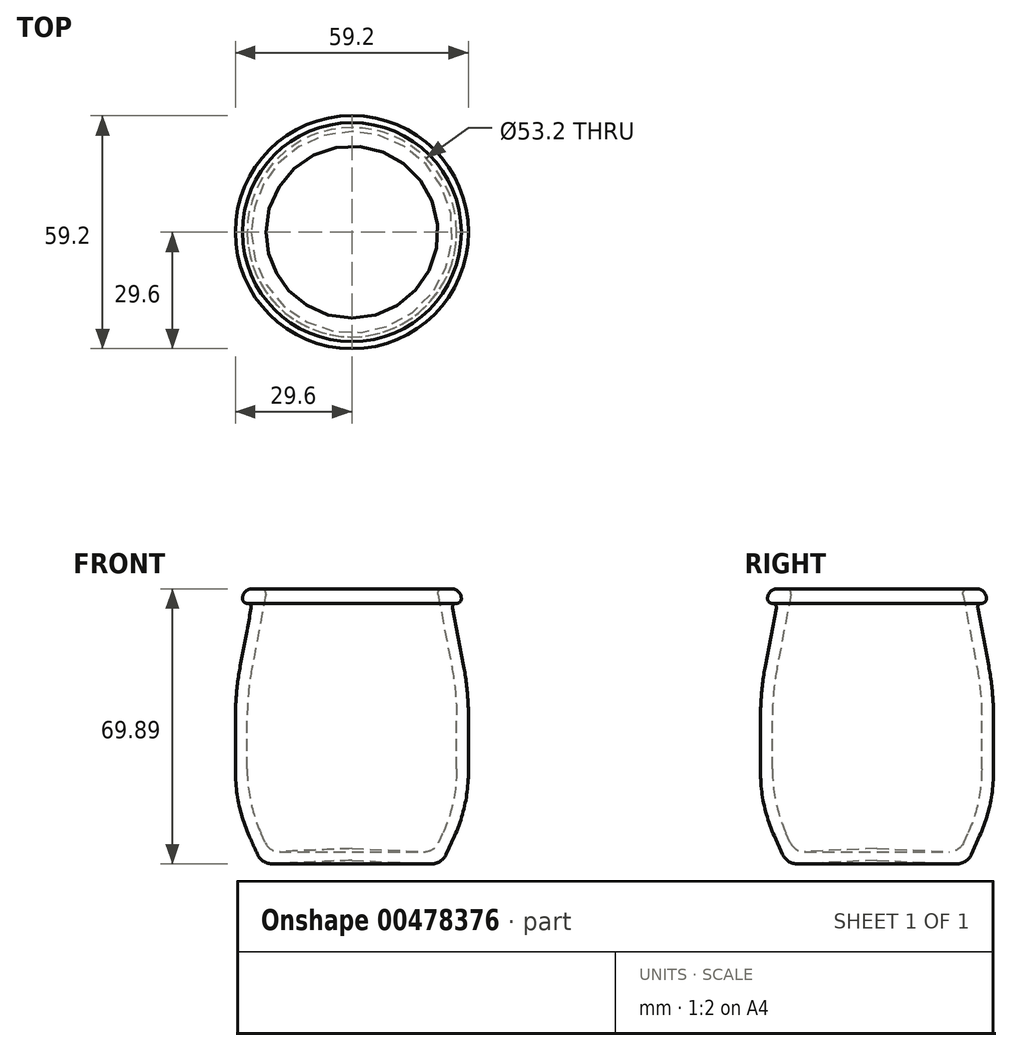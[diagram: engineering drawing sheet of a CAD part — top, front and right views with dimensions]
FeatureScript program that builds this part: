
annotation { "Feature Type Name" : "Feature", "Feature Type Description" : "" }
export const myFeature = defineFeature(function(context is Context, id is Id, definition is map)
    precondition{}
    {
        {
            var Q0;
            Q0=qCreatedBy(makeId("Front.planeOp"),FACE);
            var sketch = newSketch(context, id + "F0", { "sketchPlane" : qUnion([Q0])});
            skLineSegment(sketch, "E0.bottom", {"start": v(-27.8, 70) * mm, "end": v(-21.6, 70) * mm});
            skLineSegment(sketch, "E0.top", {"start": v(-27.8, 66.3) * mm, "end": v(-25.35, 66.3) * mm});
            skLineSegment(sketch, "E0.left", {"start": v(-27.8, 70) * mm, "end": v(-27.8, 66.3) * mm});
            skLineSegment(sketch, "E0.right", {"start": v(27.8, 70) * mm, "end": v(27.8, 66.3) * mm});
            skLineSegment(sketch, "E1.left", {"start": v(-29.6, 43.9) * mm, "end": v(-29.6, 15) * mm});
            skLineSegment(sketch, "E1.right", {"start": v(29.6, 43.9) * mm, "end": v(29.6, 15) * mm});
            skLineSegment(sketch, "E2", {"start": v(-25.35, 66.3) * mm, "end": v(-29.6, 43.9) * mm});
            skLineSegment(sketch, "E3", {"start": v(25.35, 66.3) * mm, "end": v(29.6, 43.9) * mm});
            skLineSegment(sketch, "E4", {"start": v(-29.6, 15) * mm, "end": v(-22.85, 0) * mm});
            skLineSegment(sketch, "E5", {"start": v(22.85, 0) * mm, "end": v(29.6, 15) * mm});
            skLineSegment(sketch, "E6.trimOffspring", {"start": v(25.35, 66.3) * mm, "end": v(27.8, 66.3) * mm});
            skLineSegment(sketch, "E7", {"start": v(0, 70) * mm, "end": v(0, 1) * mm, "construction": true});
            skLineSegment(sketch, "E8", {"start": v(-22.85, 0) * mm, "end": v(0, 1) * mm});
            skLineSegment(sketch, "E9", {"start": v(0, 1) * mm, "end": v(22.85, 0) * mm});
            skLineSegment(sketch, "E10.0", {"start": v(-21.6, 70) * mm, "end": v(-26.6, 43.62) * mm});
            skLineSegment(sketch, "E10.1", {"start": v(-26.6, 43.62) * mm, "end": v(-26.6, 15.64) * mm});
            skLineSegment(sketch, "E10.3", {"start": v(-26.6, 15.64) * mm, "end": v(-20.95, 3.09) * mm});
            skLineSegment(sketch, "E10.4", {"start": v(-20.95, 3.09) * mm, "end": v(0, 4) * mm});
            skLineSegment(sketch, "E10.5", {"start": v(21.6, 70) * mm, "end": v(26.6, 43.62) * mm});
            skLineSegment(sketch, "E10.6", {"start": v(26.6, 43.62) * mm, "end": v(26.6, 15.64) * mm});
            skLineSegment(sketch, "E10.7", {"start": v(20.95, 3.09) * mm, "end": v(26.6, 15.64) * mm});
            skLineSegment(sketch, "E10.8", {"start": v(0, 4) * mm, "end": v(20.95, 3.09) * mm});
            skLineSegment(sketch, "E11", {"start": v(-29.6, 29.45) * mm, "end": v(-26.6, 29.45) * mm, "construction": true});
            skLineSegment(sketch, "E12", {"start": v(-26.22, 7.5) * mm, "end": v(-23.49, 8.73) * mm, "construction": true});
            skLineSegment(sketch, "E13", {"start": v(-27.47, 55.1) * mm, "end": v(-24.53, 54.54) * mm, "construction": true});
            skLineSegment(sketch, "E14", {"start": v(-11.42, 0.5) * mm, "end": v(-11.56, 3.5) * mm, "construction": true});
            skLineSegment(sketch, "E15.trimOffspring", {"start": v(21.6, 70) * mm, "end": v(27.8, 70) * mm});
            skLineSegment(sketch, "E16", {"start": v(0, 1) * mm, "end": v(0, 4) * mm});
            skSolve(sketch);
        }
        {
            var Q0;
            Q0=makeQuery(id+"F0.imprint","IMPRINT",FACE,{"disambiguationData":[TD([[makeQuery(id+"F0.imprint","IMPRINT",EDGE,{"derivedFrom":sQuery(id+"F0.wireOp",EDGE,"E0.top")}),1.0]])]});
            var Q1;
            Q1=sQuery(id+"F0.wireOp",EDGE,"E7");
            revolve(context, id + "F1", {"entities" : qUnion([Q0]), "axis" : qUnion([Q1]), "revolveType" : RevolveType.FULL});
        }
        {
            var Q0;
            Q0=makeQuery(id+"F1.opRevolve","SWEPT_EDGE",EDGE,{"disambiguationData":[OSD([sQuery(id+"F0.wireOp",EDGE,"E0.bottom"),sQuery(id+"F0.wireOp",EDGE,"E0.left")])]});
            fillet(context, id + "F2", {"entities" : qUnion([Q0]), "radius" : 2.5 * mm, "tangentPropagation" : true, "allowEdgeOverflow" : false});
        }
        {
            var Q0;
            Q0=makeQuery(id+"F1.opRevolve","SWEPT_EDGE",EDGE,{"disambiguationData":[OSD([sQuery(id+"F0.wireOp",EDGE,"E0.top"),sQuery(id+"F0.wireOp",EDGE,"E0.left")])]});
            var Q1;
            Q1=makeQuery(id+"F1.opRevolve","SWEPT_EDGE",EDGE,{"disambiguationData":[OSD([sQuery(id+"F0.wireOp",EDGE,"E0.bottom"),sQuery(id+"F0.wireOp",EDGE,"E10.0")])]});
            fillet(context, id + "F3", {"entities" : qUnion([Q0, Q1]), "radius" : 1.2 * mm, "tangentPropagation" : true, "allowEdgeOverflow" : false});
        }
        {
            var Q0;
            Q0=makeQuery(id+"F1.opRevolve","SWEPT_EDGE",EDGE,{"disambiguationData":[OSD([sQuery(id+"F0.wireOp",EDGE,"E0.top"),sQuery(id+"F0.wireOp",EDGE,"E2")])]});
            fillet(context, id + "F4", {"entities" : qUnion([Q0]), "radius" : 1 * mm, "tangentPropagation" : true, "allowEdgeOverflow" : false});
        }
        {
            var Q0;
            Q0=makeQuery(id+"F1.opRevolve","SWEPT_EDGE",EDGE,{"disambiguationData":[OSD([sQuery(id+"F0.wireOp",EDGE,"E1.left"),sQuery(id+"F0.wireOp",EDGE,"E2")])]});
            var Q1;
            Q1=makeQuery(id+"F1.opRevolve","SWEPT_EDGE",EDGE,{"disambiguationData":[OSD([sQuery(id+"F0.wireOp",EDGE,"E10.0"),sQuery(id+"F0.wireOp",EDGE,"E10.1")])]});
            fillet(context, id + "F5", {"entities" : qUnion([Q0, Q1]), "radius" : 70 * mm, "tangentPropagation" : true, "allowEdgeOverflow" : false});
        }
        {
            var Q0;
            Q0=makeQuery(id+"F1.opRevolve","SWEPT_EDGE",EDGE,{"disambiguationData":[OSD([sQuery(id+"F0.wireOp",EDGE,"E1.left"),sQuery(id+"F0.wireOp",EDGE,"E4")])]});
            var Q1;
            Q1=makeQuery(id+"F1.opRevolve","SWEPT_EDGE",EDGE,{"disambiguationData":[OSD([sQuery(id+"F0.wireOp",EDGE,"E10.1"),sQuery(id+"F0.wireOp",EDGE,"E10.3")])]});
            fillet(context, id + "F6", {"entities" : qUnion([Q0, Q1]), "radius" : 40 * mm, "tangentPropagation" : true, "allowEdgeOverflow" : false});
        }
        {
            var Q0;
            Q0=makeQuery(id+"F1.opRevolve","SWEPT_EDGE",EDGE,{"disambiguationData":[OSD([sQuery(id+"F0.wireOp",EDGE,"loDSuiBu-uObt-K6Jt-In26-tVxjmKd9gQO9.bottom"),sQuery(id+"F0.wireOp",EDGE,"E4")])]});
            var Q1;
            Q1=makeQuery(id+"F1.opRevolve","SWEPT_EDGE",EDGE,{"disambiguationData":[OSD([sQuery(id+"F0.wireOp",EDGE,"E10.3"),sQuery(id+"F0.wireOp",EDGE,"E10.4")])]});
            fillet(context, id + "F7", {"entities" : qUnion([Q0, Q1]), "radius" : 4 * mm, "tangentPropagation" : true, "allowEdgeOverflow" : false});
        }
    });
